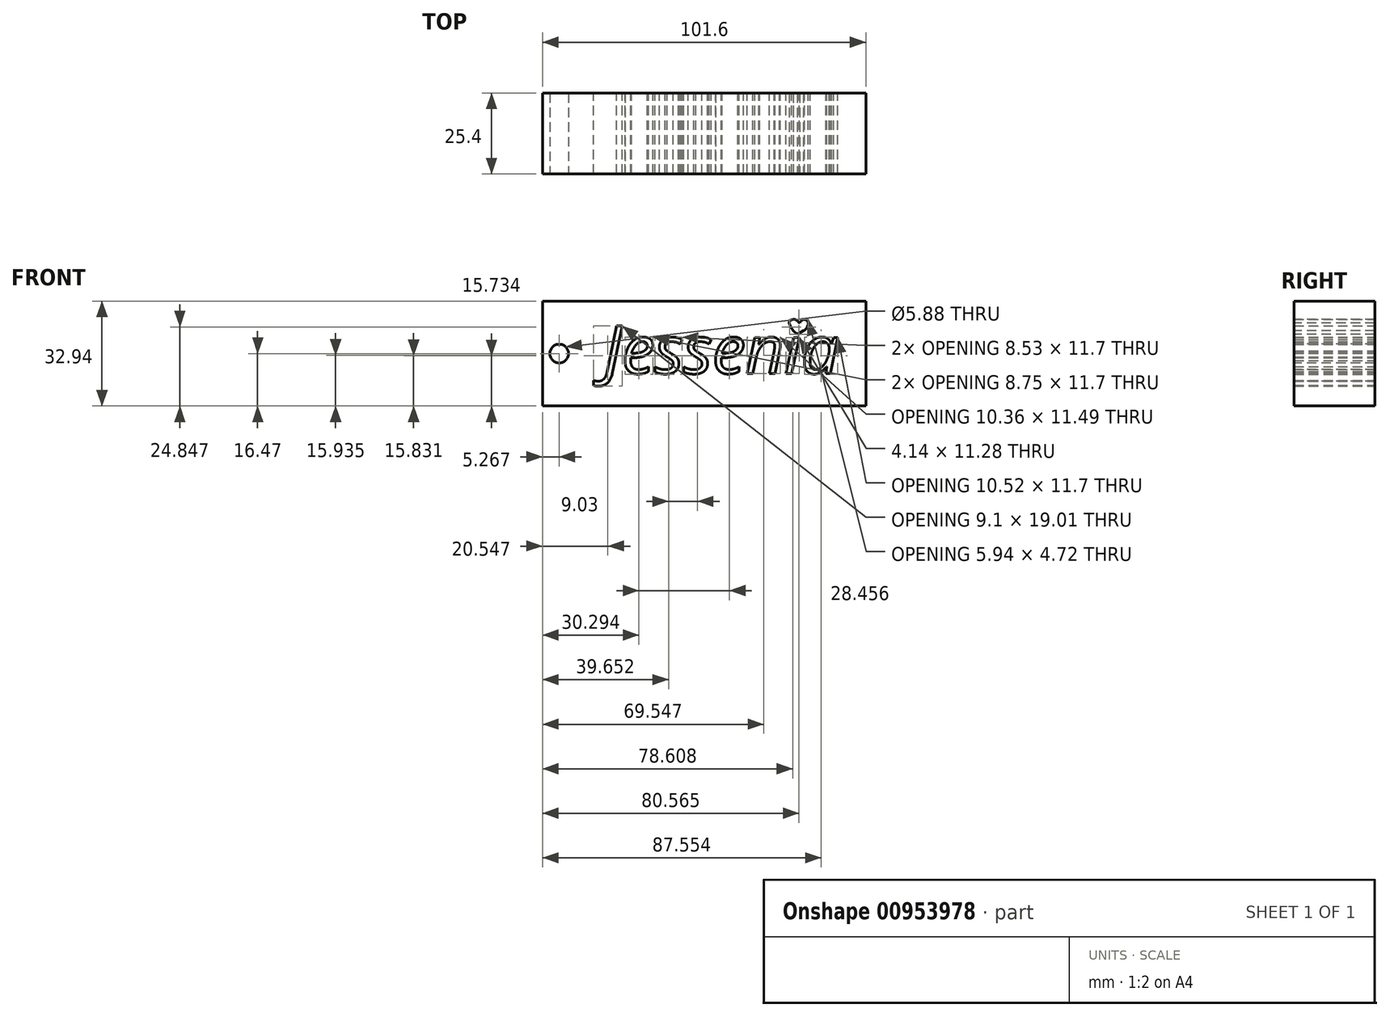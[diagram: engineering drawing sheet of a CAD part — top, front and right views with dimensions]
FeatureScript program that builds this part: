
annotation { "Feature Type Name" : "Feature", "Feature Type Description" : "" }
export const myFeature = defineFeature(function(context is Context, id is Id, definition is map)
    precondition{}
    {
        {
            var Q0;
            Q0=qCreatedBy(makeId("Front.planeOp"),FACE);
            var sketch = newSketch(context, id + "F0", { "sketchPlane" : qUnion([Q0])});
            skLineSegment(sketch, "E0.bottom", {"start": v(52.97, 16.47) * mm, "end": v(-48.63, 16.47) * mm});
            skLineSegment(sketch, "E0.top", {"start": v(52.97, -16.47) * mm, "end": v(-48.63, -16.47) * mm});
            skLineSegment(sketch, "E0.left", {"start": v(52.97, 16.47) * mm, "end": v(52.97, -16.47) * mm});
            skLineSegment(sketch, "E0.right", {"start": v(-48.63, 16.47) * mm, "end": v(-48.63, -16.47) * mm});
            skPoint(sketch, "E0.middle", {"position": v(2.17, 0) * mm});
            skSolve(sketch);
        }
        {
            var Q0;
            Q0=makeQuery(id+"F0.imprint","IMPRINT",FACE,{"disambiguationData":[TD([[makeQuery(id+"F0.imprint","IMPRINT",EDGE,{"derivedFrom":sQuery(id+"F0.wireOp",EDGE,"E0.bottom")}),1.0]])]});
            var sketch = newSketch(context, id + "F1", { "sketchPlane" : qUnion([Q0])});
            skText(sketch, "E1", { "text": "Jessenia", "fontName": "OpenSans-Italic.ttf"});
            const initialGuessF1  = {"E1": [-0.02935, -0.00628, 1, 0, 0.01518]};
            skSetInitialGuess(sketch, initialGuessF1);
            skSolve(sketch);
        }
        {
            var Q0;
            Q0=makeQuery(id+"F0.imprint","IMPRINT",FACE,{"disambiguationData":[TD([[makeQuery(id+"F0.imprint","IMPRINT",EDGE,{"derivedFrom":sQuery(id+"F0.wireOp",EDGE,"E0.bottom")}),1.0]])]});
            extrude(context, id + "F2", {"entities" : qUnion([Q0]), "depth" : 25.4 * mm, "offsetDistance" : 25.4 * mm});
        }
        {
            var Q0;
            Q0 = qSketchRegion(id + "F1", true);
            extrude(context, id + "F3", {"entities" : qUnion([Q0]), "operationType" : NewBodyOperationType.REMOVE, "depth" : 25.4 * mm, "offsetDistance" : 25.4 * mm});
        }
        {
            var Q0;
            {var subQ0=sQuery(id+"F0.wireOp",EDGE,"E0.left");var subQ1=sQuery(id+"F0.wireOp",EDGE,"E0.top");var subQ2=sQuery(id+"F0.wireOp",EDGE,"E0.right");var subQ3=sQuery(id+"F0.wireOp",EDGE,"E0.bottom");Q0=makeQuery(id+"F3.boolean.opBoolean","SPLIT",FACE,{"disambiguationData":[TD([makeQuery(id+"F2.opExtrude","SWEPT_FACE",FACE,{"disambiguationData":[OSD([subQ3])]})])],"derivedFrom":makeQuery(id+"F2.opExtrude","CAP_FACE",FACE,{"disambiguationData":[OSD([subQ3,subQ1,subQ0,subQ2])],"isStart":false})});}
            var sketch = newSketch(context, id + "F4", { "sketchPlane" : qUnion([Q0])});
            skSolve(sketch);
        }
        {
            var Q0;
            Q0=makeQuery(id+"F4.imprint","IMPRINT",FACE,{"disambiguationData":[TD([[makeQuery(id+"F4.imprint","IMPRINT",EDGE,{"derivedFrom":makeQuery(id+"F2.opExtrude","CAP_EDGE",EDGE,{"disambiguationData":[OSD([sQuery(id+"F0.wireOp",EDGE,"E0.bottom")])],"isStart":false})}),1.0]])]});
            var sketch = newSketch(context, id + "F5", { "sketchPlane" : qUnion([Q0])});
            skPoint(sketch, "E2", {"position": v(32.13, 9.59) * mm});
            skPoint(sketch, "E3", {"position": v(31.46, 6.02) * mm});
            skPoint(sketch, "E4", {"position": v(33.4, 7.22) * mm});
            skPoint(sketch, "E5", {"position": v(30.15, 7.22) * mm});
            skPoint(sketch, "E6", {"position": v(29, 10.1) * mm});
            skPoint(sketch, "E7", {"position": v(30.7, 10.7) * mm});
            skPoint(sketch, "E8", {"position": v(33.31, 10.68) * mm});
            skPoint(sketch, "E9", {"position": v(34.88, 9.79) * mm});
            skFitSpline(sketch, "E10", {"points": [v(32.13, 9.59) * mm, v(30.7, 10.7) * mm, v(29, 10.1) * mm, v(30.15, 7.22) * mm], "startDerivative": vector(-3.96, 4.33) * mm, "endDerivative": vector(5.78, -8.26) * mm});
            skFitSpline(sketch, "E11", {"points": [v(32.13, 9.59) * mm, v(33.31, 10.68) * mm, v(34.88, 9.79) * mm, v(33.4, 7.22) * mm], "startDerivative": vector(3.48, 4.64) * mm, "endDerivative": vector(-6.6, -2.48) * mm});
            skLineSegment(sketch, "E12", {"start": v(30.15, 7.22) * mm, "end": v(31.46, 6.02) * mm});
            skLineSegment(sketch, "E13", {"start": v(33.4, 7.22) * mm, "end": v(31.46, 6.02) * mm});
            skSolve(sketch);
        }
        {
            var Q0;
            Q0 = qSketchRegion(id + "F5", true);
            extrude(context, id + "F6", {"entities" : qUnion([Q0]), "operationType" : NewBodyOperationType.REMOVE, "oppositeDirection" : true, "depth" : 25.4 * mm, "offsetDistance" : 25.4 * mm});
        }
        {
            var Q0;
            Q0=makeQuery(id+"F4.imprint","IMPRINT",FACE,{"disambiguationData":[TD([[makeQuery(id+"F4.imprint","IMPRINT",EDGE,{"derivedFrom":makeQuery(id+"F2.opExtrude","CAP_EDGE",EDGE,{"disambiguationData":[OSD([sQuery(id+"F0.wireOp",EDGE,"E0.bottom")])],"isStart":false})}),1.0]])]});
            var sketch = newSketch(context, id + "F7", { "sketchPlane" : qUnion([Q0])});
            skCircle(sketch, "E14", {"center": v(-43.36, 0) * mm, "radius": 2.94 * mm});
            skSolve(sketch);
        }
        {
            var Q0;
            Q0=makeQuery(id+"F7.imprint","IMPRINT",FACE,{"disambiguationData":[TD([[makeQuery(id+"F7.imprint","IMPRINT",EDGE,{"derivedFrom":sQuery(id+"F7.wireOp",EDGE,"E14")}),1.0]])]});
            extrude(context, id + "F8", {"entities" : qUnion([Q0]), "operationType" : NewBodyOperationType.REMOVE, "oppositeDirection" : true, "depth" : 25.4 * mm, "offsetDistance" : 25.4 * mm});
        }
    });
